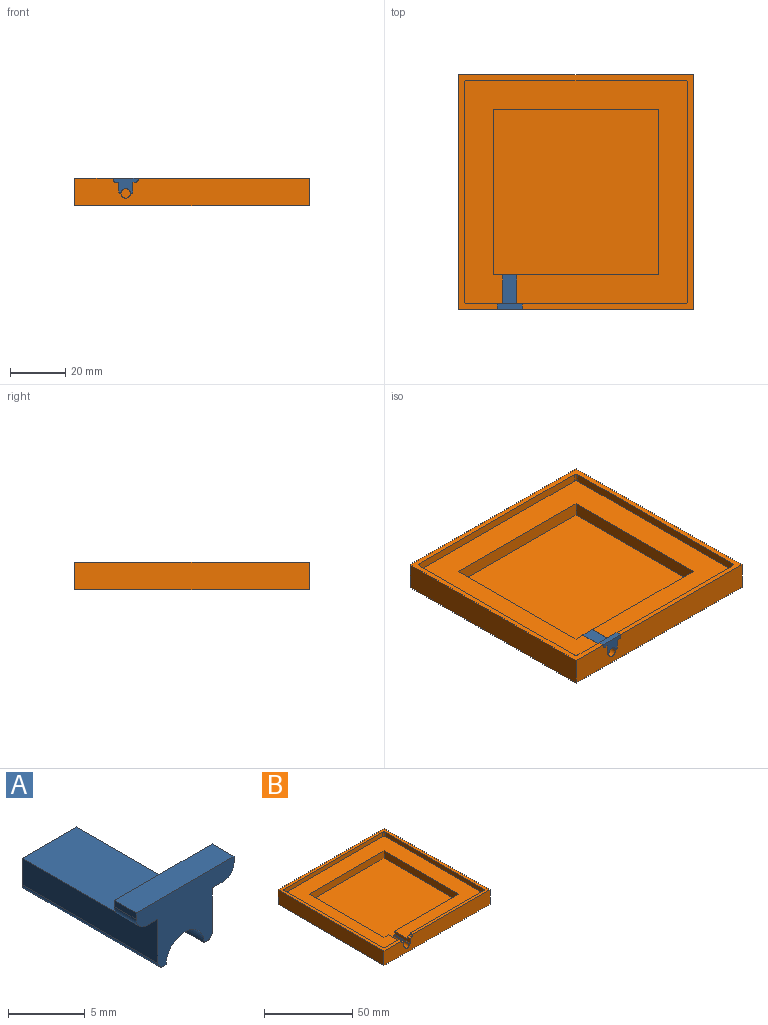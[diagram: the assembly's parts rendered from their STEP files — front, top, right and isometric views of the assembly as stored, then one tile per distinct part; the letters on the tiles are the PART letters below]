
ASSEMBLY  parts=2 mates=1
PART A: 18 faces, bbox 9x12.5x5.5 mm
  f0: plane 9x2.9mm, normal (0,1,0), area 20.1mm2, adj f1,f4,f7,f8,f9,f10,f11,f12
  f1: plane 12.5x3.5mm, normal (1,0,0), area 29.1mm2, adj f0,f3,f8,f14,f16,f17
  f2: plane 12.5x0.25mm, normal (0,0,-1), area 3.1mm2, adj f3,f5,f15,f17
  f3: plane 9x5.5mm, normal (0,-1,0), area 28.2mm2, adj f1,f2,f4,f5,f6,f7,f8,f9
  f4: plane 12.5x3.5mm, normal (-1,0,0), area 29.1mm2, adj f0,f3,f13,f15,f16,f17
  f5: cylinder r=1.75mm len=12.5mm, axis (0,1,0), area 68.7mm2, adj f2,f3,f6,f17
  f6: plane 12.5x0.25mm, normal (0,0,-1), area 3.1mm2, adj f3,f5,f14,f17
  f7: plane 9x2mm, normal (0,0,1), area 18mm2, adj f0,f3,f10,f11
  f8: plane 2x1mm, normal (0,0,-1), area 2mm2, adj f0,f1,f3,f9
  f9: cylinder r=1mm len=2mm, axis (0,-1,0), area 3.1mm2, adj f0,f3,f8,f10
  f10: plane 2x0.5mm, normal (1,0,0), area 1mm2, adj f0,f3,f7,f9
  f11: plane 2x0.5mm, normal (-1,0,0), area 1mm2, adj f0,f3,f7,f12
  f12: cylinder r=1mm len=2mm, axis (0,-1,0), area 3.1mm2, adj f0,f3,f11,f13
  f13: plane 2x1mm, normal (0,0,-1), area 2mm2, adj f0,f3,f4,f12
  f14: cylinder r=0.5mm len=12.5mm, axis (0,-1,0), area 9.8mm2, adj f1,f3,f6,f17
  f15: cylinder r=0.5mm len=12.5mm, axis (0,-1,0), area 9.8mm2, adj f2,f3,f4,f17
  f16: plane 10.5x5mm, normal (0,0,1), area 52.5mm2, adj f0,f1,f4,f17
  f17: plane 5x2.6mm, normal (0,1,0), area 8.1mm2, adj f1,f2,f4,f5,f6,f14,f15,f16
PART B: 34 faces, bbox 85x85x10 mm
  f0: plane 85x85mm, normal (0,0,1), area 646.9mm2, adj f1,f2,f4,f5,f6,f8,f9,f10
  f1: plane 85x10mm, normal (0,-1,0), area 812.2mm2, adj f0,f4,f5,f7,f21,f22,f23,f24
  f2: plane 61x3mm, normal (0,1,0), area 180.2mm2, adj f0,f3,f15,f30,f31,f32,f33
  f3: plane 81x81mm, normal (0,0,1), area 2907.6mm2, adj f2,f8,f9,f10,f11,f12,f13,f14
  f4: plane 85x10mm, normal (-1,0,0), area 850mm2, adj f0,f1,f6,f7
  f5: plane 85x10mm, normal (1,0,0), area 850mm2, adj f0,f1,f6,f7
  f6: plane 85x10mm, normal (0,1,0), area 850mm2, adj f0,f4,f5,f7
  f7: plane 85x85mm, normal (0,0,-1), area 7225mm2, adj f1,f4,f5,f6
  f8: plane 79x3mm, normal (-1,0,0), area 237mm2, adj f0,f3,f9,f15
  f9: cylinder r=1mm len=3mm, axis (0,0,1), area 4.7mm2, adj f0,f3,f8,f10
  f10: plane 79x3mm, normal (0,-1,0), area 237mm2, adj f0,f3,f9,f11
  f11: cylinder r=1mm len=3mm, axis (0,0,1), area 4.7mm2, adj f0,f3,f10,f12
  f12: plane 79x3mm, normal (1,0,0), area 237mm2, adj f0,f3,f11,f13
  f13: cylinder r=1mm len=3mm, axis (0,0,1), area 4.7mm2, adj f0,f3,f12,f14
  f14: plane 13x3mm, normal (0,1,0), area 36.2mm2, adj f0,f3,f13,f21,f22,f23,f24
  f15: cylinder r=1mm len=3mm, axis (0,0,1), area 4.7mm2, adj f0,f2,f3,f8
  f16: plane 60x5mm, normal (-1,0,0), area 300mm2, adj f3,f17,f19,f20
  f17: plane 60x5mm, normal (0,-1,0), area 300mm2, adj f3,f16,f18,f20
  f18: plane 60x5mm, normal (1,0,0), area 300mm2, adj f3,f17,f19,f20
  f19: plane 60x5mm, normal (0,1,0), area 282.8mm2, adj f3,f16,f18,f20,f24,f25,f26,f27
  f20: plane 60x60mm, normal (0,0,1), area 3600mm2, adj f16,f17,f18,f19
  f21: plane 2x0.5mm, normal (1,0,0), area 1mm2, adj f0,f1,f14,f22
  f22: cylinder r=1mm len=2mm, axis (0,-1,0), area 3.1mm2, adj f1,f14,f21,f23
  f23: plane 2x1mm, normal (0,0,1), area 2mm2, adj f1,f14,f22,f24
  f24: plane 12.5x3.5mm, normal (1,0,0), area 28mm2, adj f1,f3,f14,f19,f23,f25
  f25: cylinder r=0.5mm len=12.5mm, axis (0,-1,0), area 9.8mm2, adj f1,f19,f24,f26
  f26: plane 12.5x0.25mm, normal (0,0,1), area 3.1mm2, adj f1,f19,f25,f27
  f27: cylinder r=1.75mm len=12.5mm, axis (0,-1,0), area 68.7mm2, adj f1,f19,f26,f28
  f28: plane 12.5x0.25mm, normal (0,0,1), area 3.1mm2, adj f1,f19,f27,f29
  f29: cylinder r=0.5mm len=12.5mm, axis (0,-1,0), area 9.8mm2, adj f1,f19,f28,f30
  f30: plane 12.5x3.5mm, normal (-1,0,0), area 28mm2, adj f1,f2,f3,f19,f29,f31
  f31: plane 2x1mm, normal (0,0,1), area 2mm2, adj f1,f2,f30,f32
  f32: cylinder r=1mm len=2mm, axis (0,-1,0), area 3.1mm2, adj f1,f2,f31,f33
  f33: plane 2x0.5mm, normal (-1,0,0), area 1mm2, adj f0,f1,f2,f32
PLACE A t=(-24,-40.5,11)mm
PLACE B at identity
MATE revolute A.f5 <-> B.f27  axis (0,-1,0) through (-24,-42.5,4.5)mm
